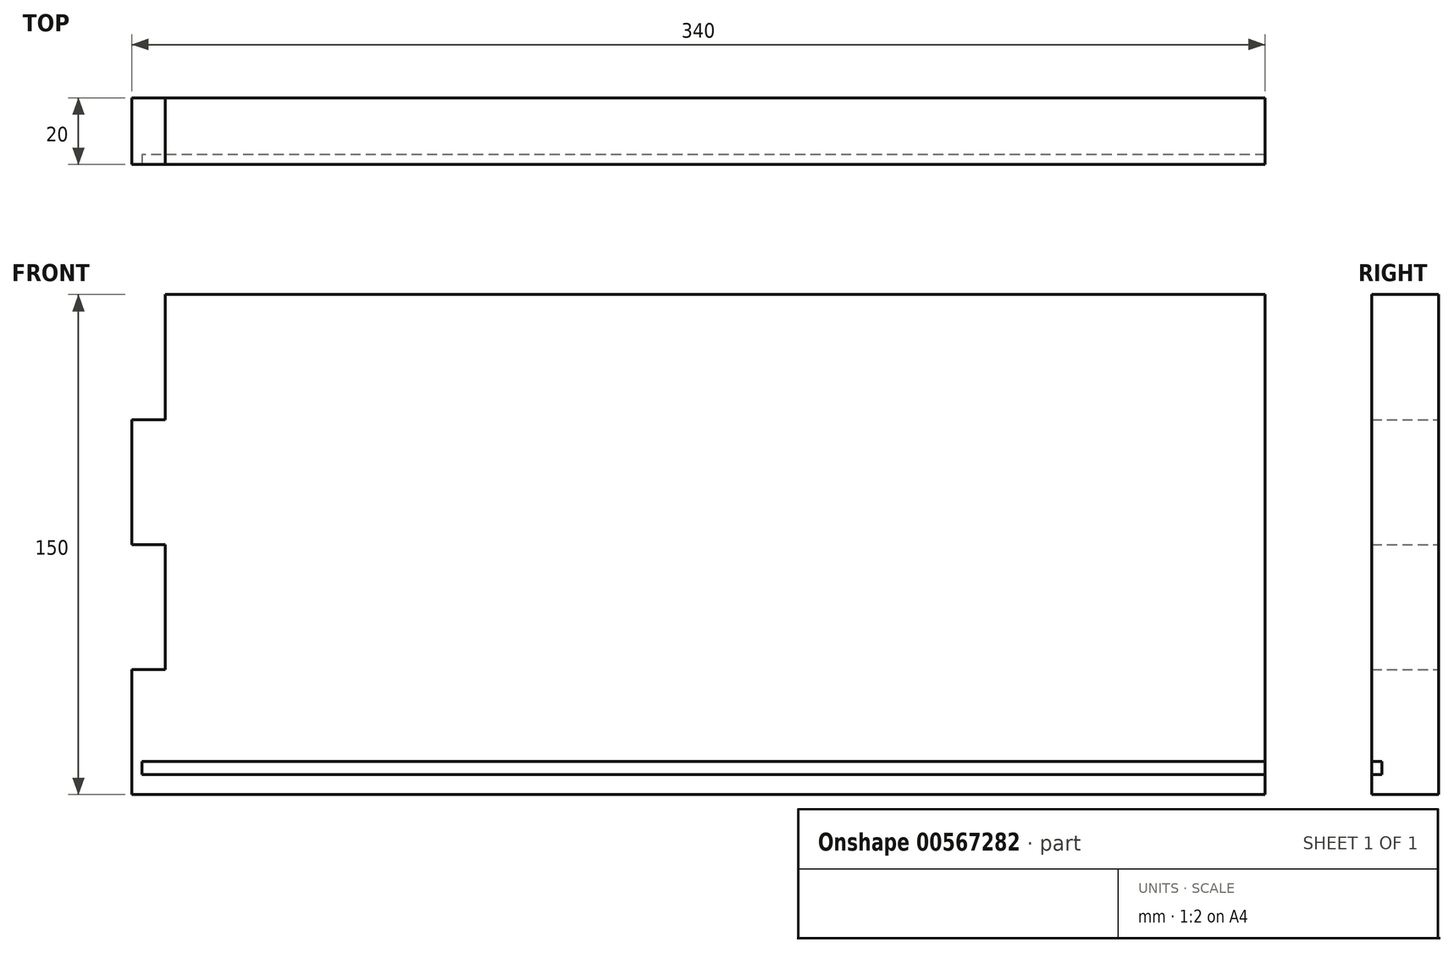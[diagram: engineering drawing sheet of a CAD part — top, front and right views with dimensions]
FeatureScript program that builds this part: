
annotation { "Feature Type Name" : "Feature", "Feature Type Description" : "" }
export const myFeature = defineFeature(function(context is Context, id is Id, definition is map)
    precondition{}
    {
        {
            var Q0;
            Q0=qCreatedBy(makeId("Front.planeOp"),FACE);
            var sketch = newSketch(context, id + "F0", { "sketchPlane" : qUnion([Q0])});
            skLineSegment(sketch, "E0.bottom", {"start": v(298.64, 141.53) * mm, "end": v(-31.36, 141.53) * mm});
            skLineSegment(sketch, "E0.top", {"start": v(298.64, -8.47) * mm, "end": v(-41.36, -8.47) * mm});
            skLineSegment(sketch, "E0.left", {"start": v(298.64, 141.53) * mm, "end": v(298.64, -8.47) * mm});
            skLineSegment(sketch, "E1", {"start": v(-31.36, 141.53) * mm, "end": v(-31.36, 104.03) * mm});
            skLineSegment(sketch, "E2", {"start": v(-31.36, 66.53) * mm, "end": v(-41.36, 66.53) * mm});
            skLineSegment(sketch, "E3", {"start": v(-31.36, 104.03) * mm, "end": v(-41.36, 104.03) * mm});
            skLineSegment(sketch, "E4", {"start": v(-31.36, 29.03) * mm, "end": v(-41.36, 29.03) * mm});
            skLineSegment(sketch, "E5.trimOffspring", {"start": v(-31.36, 66.53) * mm, "end": v(-31.36, 29.03) * mm});
            skPoint(sketch, "E6.orphan", {"position": v(-51.36, 141.53) * mm});
            skLineSegment(sketch, "E7", {"start": v(-41.36, 104.03) * mm, "end": v(-41.36, 66.53) * mm});
            skLineSegment(sketch, "E8", {"start": v(-41.36, 29.03) * mm, "end": v(-41.36, -8.47) * mm});
            skPoint(sketch, "E9.orphan", {"position": v(-51.36, 104.03) * mm});
            skPoint(sketch, "E10.orphan", {"position": v(-51.36, 66.53) * mm});
            skPoint(sketch, "E11.trimOffspring.start.orphan", {"position": v(-51.36, 29.03) * mm});
            skSolve(sketch);
        }
        {
            var Q0;
            Q0=makeQuery(id+"F0.imprint","IMPRINT",FACE,{"disambiguationData":[TD([[makeQuery(id+"F0.imprint","IMPRINT",EDGE,{"derivedFrom":sQuery(id+"F0.wireOp",EDGE,"E0.bottom")}),1.0]])]});
            extrude(context, id + "F1", {"entities" : qUnion([Q0]), "depth" : 20 * mm, "offsetDistance" : 25 * mm});
        }
        {
            var Q0;
            Q0=makeQuery(id+"F1.opExtrude","CAP_FACE",FACE,{"disambiguationData":[OSD([sQuery(id+"F0.wireOp",EDGE,"E0.bottom"),sQuery(id+"F0.wireOp",EDGE,"E0.top"),sQuery(id+"F0.wireOp",EDGE,"E0.left"),sQuery(id+"F0.wireOp",EDGE,"E1"),sQuery(id+"F0.wireOp",EDGE,"E2"),sQuery(id+"F0.wireOp",EDGE,"E3"),sQuery(id+"F0.wireOp",EDGE,"E4"),sQuery(id+"F0.wireOp",EDGE,"E5.trimOffspring"),sQuery(id+"F0.wireOp",EDGE,"E7"),sQuery(id+"F0.wireOp",EDGE,"E8")])],"isStart":false});
            var sketch = newSketch(context, id + "F2", { "sketchPlane" : qUnion([Q0])});
            skLineSegment(sketch, "E12", {"start": v(298.64, 1.53) * mm, "end": v(-38.36, 1.53) * mm});
            skLineSegment(sketch, "E13", {"start": v(298.64, -2.47) * mm, "end": v(-38.36, -2.47) * mm});
            skLineSegment(sketch, "E14", {"start": v(-38.36, -2.47) * mm, "end": v(-38.36, 1.53) * mm});
            skSolve(sketch);
        }
        {
            var Q0;
            {var subQ0=sQuery(id+"F2.wireOp",EDGE,"E12");Q0=makeQuery(id+"F2.imprint","IMPRINT",FACE,{"disambiguationData":[TD([[makeQuery(id+"F2.imprint","IMPRINT",EDGE,{"derivedFrom":subQ0}),1.0]])]});}
            extrude(context, id + "F3", {"entities" : qUnion([Q0]), "operationType" : NewBodyOperationType.REMOVE, "oppositeDirection" : true, "depth" : 3 * mm, "offsetDistance" : 25 * mm});
        }
    });
